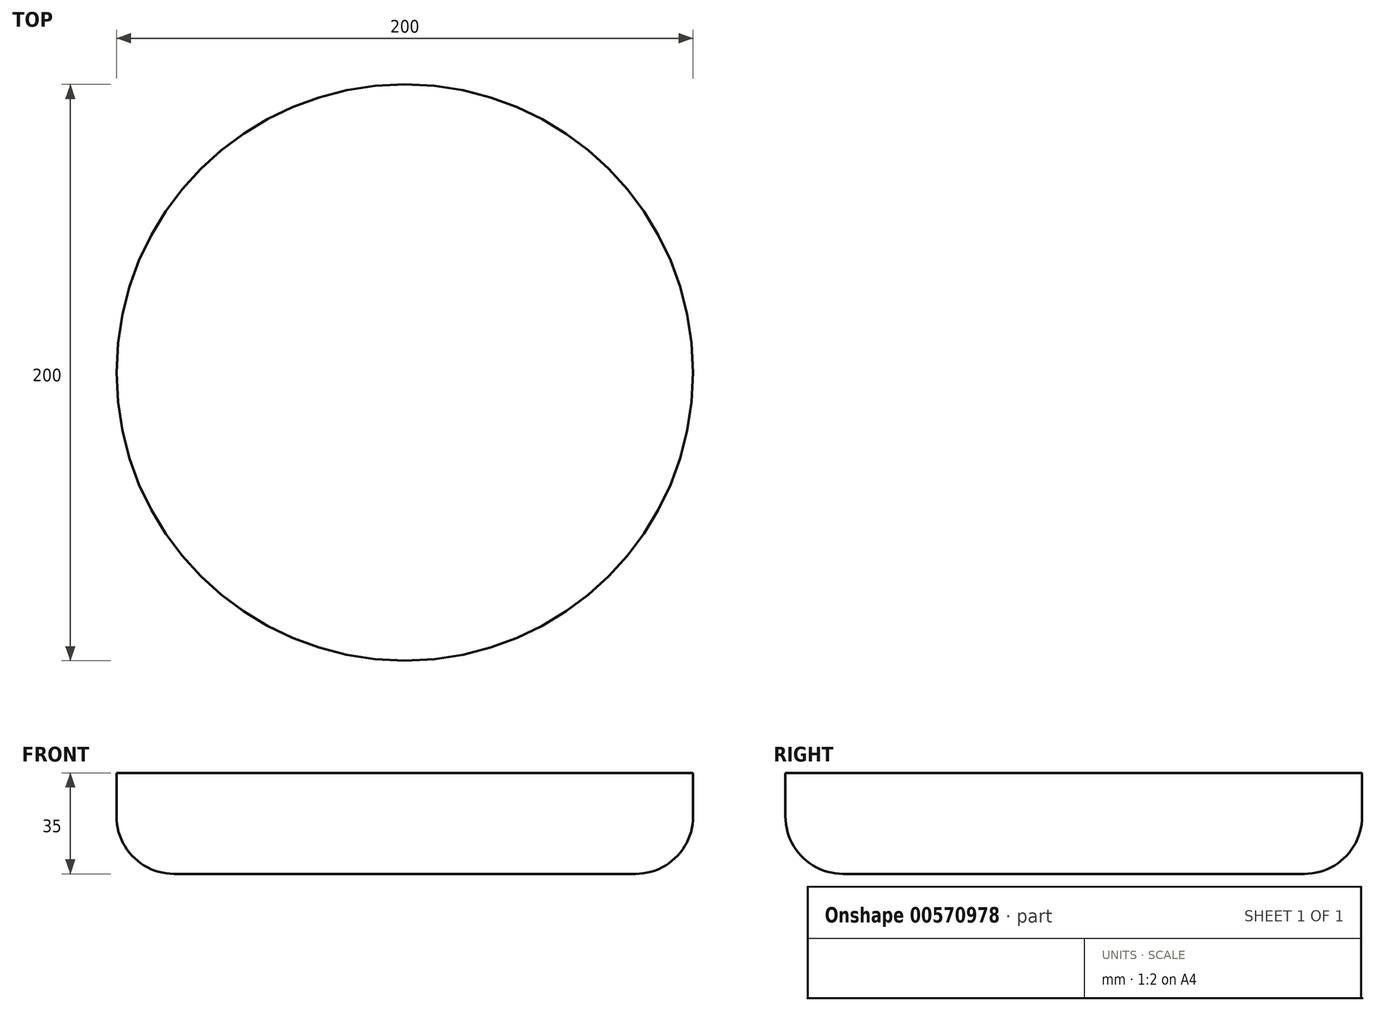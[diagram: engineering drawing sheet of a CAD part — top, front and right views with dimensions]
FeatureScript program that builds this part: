
annotation { "Feature Type Name" : "Feature", "Feature Type Description" : "" }
export const myFeature = defineFeature(function(context is Context, id is Id, definition is map)
    precondition{}
    {
        {
            var Q0;
            Q0=qCreatedBy(makeId("Top.planeOp"),FACE);
            var sketch = newSketch(context, id + "F0", { "sketchPlane" : qUnion([Q0])});
            skCircle(sketch, "E0", {"center": v(0, 0) * mm, "radius": 100 * mm});
            skSolve(sketch);
        }
        {
            var Q0;
            Q0 = qSketchRegion(id + "F0", true);
            extrude(context, id + "F1", {"entities" : qUnion([Q0]), "depth" : 35 * mm, "offsetDistance" : 25 * mm});
        }
        {
            var Q0;
            Q0=makeQuery(id+"F1.opExtrude","CAP_EDGE",EDGE,{"disambiguationData":[OSD([sQuery(id+"F0.wireOp",EDGE,"E0")])],"isStart":true});
            fillet(context, id + "F2", {"entities" : qUnion([Q0]), "radius" : 20 * mm, "tangentPropagation" : true, "allowEdgeOverflow" : false});
        }
    });
